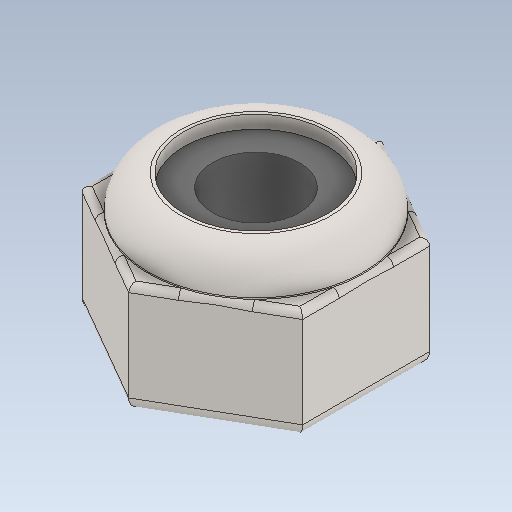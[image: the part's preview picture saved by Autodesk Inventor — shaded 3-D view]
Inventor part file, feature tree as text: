
AUTODESK INVENTOR PART (.ipt)
format: ipt  version: 2020 (Build 240168000, 168)  size: 214,016 bytes
history: native  units: in
note: dims shown in document units (in); Inventor stores cm internally (conversion verified against a paired STEP export)
features: fillet x1
ambient origin geometry x8: Origin, YZ Plane, XZ Plane, XY Plane, X Axis, Y Axis, Z Axis, Center Point
bodies: Solid1 (feature_tree)
feature tree (1):
  fillet  "Fillet6"  [1 undecoded]
note: 1 required parameter value undecoded (feature->parameter linkage not recoverable at this tier; creation-order binding heuristic only, values carry confidence <= 0.55)
